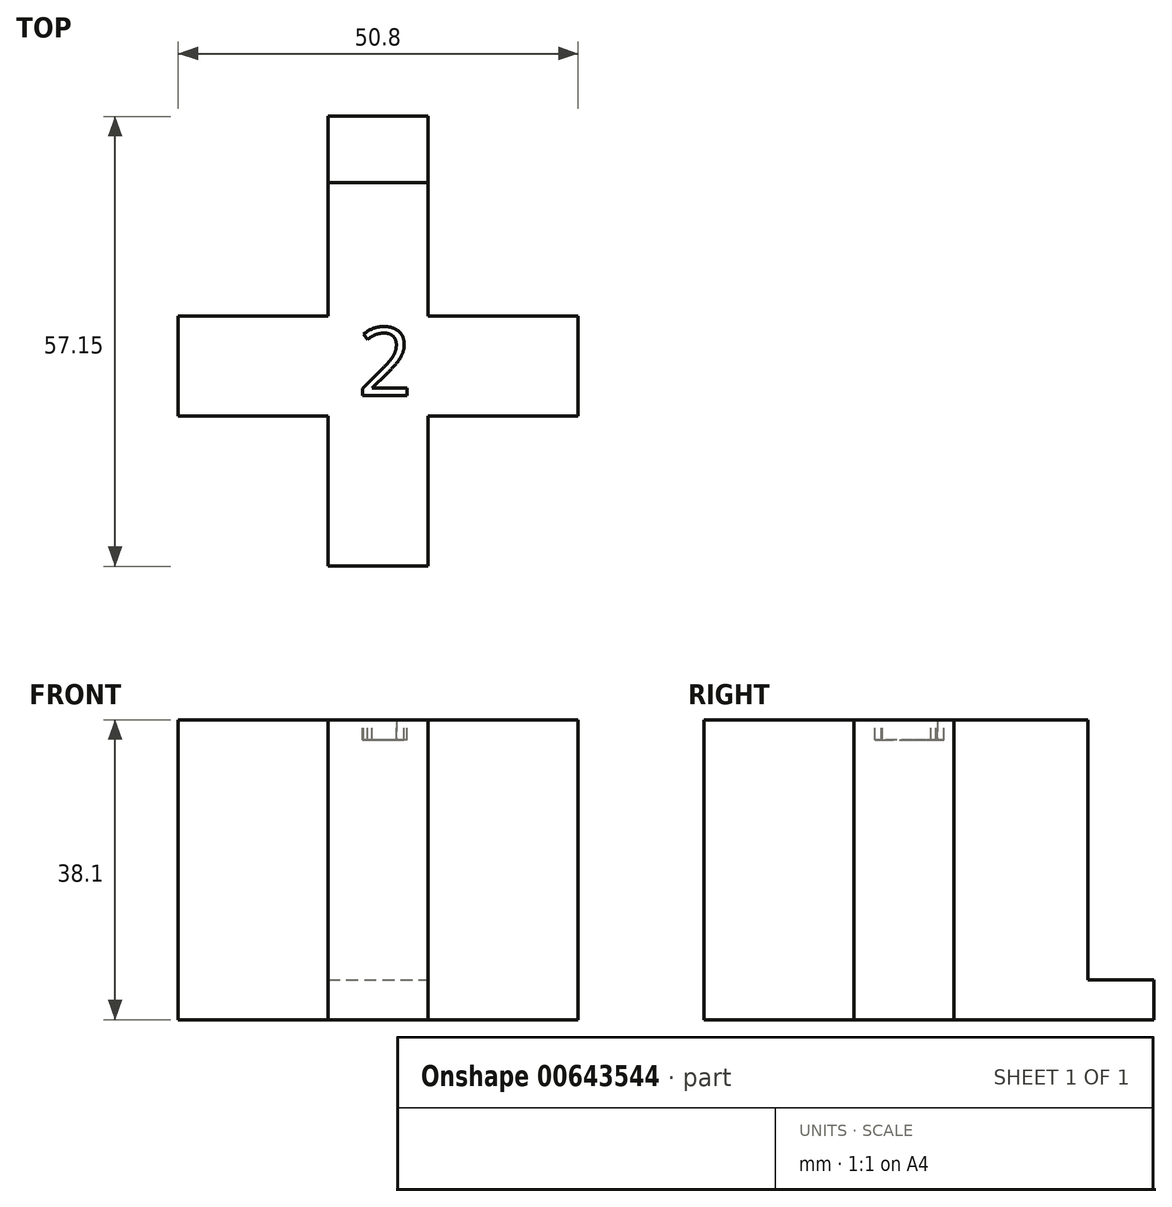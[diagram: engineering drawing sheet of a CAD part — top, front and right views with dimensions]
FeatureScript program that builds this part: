
annotation { "Feature Type Name" : "Feature", "Feature Type Description" : "" }
export const myFeature = defineFeature(function(context is Context, id is Id, definition is map)
    precondition{}
    {
        {
            var Q0;
            Q0=qCreatedBy(makeId("Top.planeOp"),FACE);
            var sketch = newSketch(context, id + "F0", { "sketchPlane" : qUnion([Q0])});
            skLineSegment(sketch, "E0.bottom", {"start": v(-43.37, 31.57) * mm, "end": v(-30.67, 31.57) * mm});
            skLineSegment(sketch, "E0.top", {"start": v(-43.37, -25.58) * mm, "end": v(-30.67, -25.58) * mm});
            skLineSegment(sketch, "E0.left", {"start": v(-43.37, 31.57) * mm, "end": v(-43.37, -25.58) * mm});
            skLineSegment(sketch, "E0.right", {"start": v(-30.67, 31.57) * mm, "end": v(-30.67, -25.58) * mm});
            skSolve(sketch);
        }
        {
            var Q0;
            Q0=qSketchRegion(id+"F0",true);
            extrude(context, id + "F1", {"entities" : qUnion([Q0]), "depth" : 5.08 * mm, "offsetDistance" : 25.4 * mm});
        }
        {
            var Q0;
            Q0=qCreatedBy(makeId("Top.planeOp"),FACE);
            var sketch = newSketch(context, id + "F2", { "sketchPlane" : qUnion([Q0])});
            skLineSegment(sketch, "E1.bottom", {"start": v(-62.42, -6.53) * mm, "end": v(-11.62, -6.53) * mm});
            skLineSegment(sketch, "E1.top", {"start": v(-62.42, 6.17) * mm, "end": v(-11.62, 6.17) * mm});
            skLineSegment(sketch, "E1.left", {"start": v(-62.42, -6.53) * mm, "end": v(-62.42, 6.17) * mm});
            skLineSegment(sketch, "E1.right", {"start": v(-11.62, -6.53) * mm, "end": v(-11.62, 6.17) * mm});
            skSolve(sketch);
        }
        {
            var Q0;
            Q0=qSketchRegion(id+"F2",true);
            extrude(context, id + "F3", {"entities" : qUnion([Q0]), "operationType" : NewBodyOperationType.ADD, "depth" : 38.1 * mm, "offsetDistance" : 25.4 * mm});
        }
        {
            var Q0;
            {var subQ0=sQuery(id+"F0.wireOp",EDGE,"E0.top");var subQ1=sQuery(id+"F0.wireOp",EDGE,"E0.left");var subQ2=sQuery(id+"F0.wireOp",EDGE,"E0.right");Q0=makeQuery(id+"F3.boolean.opBoolean","SPLIT",FACE,{"disambiguationData":[TD([makeQuery(id+"F1.opExtrude","SWEPT_FACE",FACE,{"disambiguationData":[OSD([subQ0])]})])],"derivedFrom":makeQuery(id+"F1.opExtrude","CAP_FACE",FACE,{"disambiguationData":[OSD([sQuery(id+"F0.wireOp",EDGE,"E0.bottom"),subQ0,subQ1,subQ2])],"isStart":false})});}
            var sketch = newSketch(context, id + "F4", { "sketchPlane" : qUnion([Q0])});
            skLineSegment(sketch, "E2.bottom", {"start": v(-30.67, -25.58) * mm, "end": v(-43.37, -25.58) * mm});
            skLineSegment(sketch, "E2.top", {"start": v(-30.67, 23.16) * mm, "end": v(-43.37, 23.16) * mm});
            skLineSegment(sketch, "E2.left", {"start": v(-30.67, -25.58) * mm, "end": v(-30.67, 23.16) * mm});
            skLineSegment(sketch, "E2.right", {"start": v(-43.37, -25.58) * mm, "end": v(-43.37, 23.16) * mm});
            skSolve(sketch);
        }
        {
            var Q0;
            Q0=qSketchRegion(id+"F4",true);
            extrude(context, id + "F5", {"entities" : qUnion([Q0]), "operationType" : NewBodyOperationType.ADD, "depth" : 33.02 * mm, "offsetDistance" : 25.4 * mm});
        }
        {
            var Q0;
            Q0=makeQuery(id+"F5.boolean.opBoolean","MERGE",FACE,{"derivedFrom":[makeQuery(id+"F3.opExtrude","CAP_FACE",FACE,{"disambiguationData":[OSD([sQuery(id+"F2.wireOp",EDGE,"E1.bottom"),sQuery(id+"F2.wireOp",EDGE,"E1.top"),sQuery(id+"F2.wireOp",EDGE,"E1.left"),sQuery(id+"F2.wireOp",EDGE,"E1.right")])],"isStart":false}),makeQuery(id+"F5.opExtrude","CAP_FACE",FACE,{"disambiguationData":[OSD([sQuery(id+"F4.wireOp",EDGE,"E2.bottom"),sQuery(id+"F4.wireOp",EDGE,"E2.top"),sQuery(id+"F4.wireOp",EDGE,"E2.left"),sQuery(id+"F4.wireOp",EDGE,"E2.right")])],"isStart":false})]});
            var sketch = newSketch(context, id + "F6", { "sketchPlane" : qUnion([Q0])});
            skText(sketch, "E3", { "text": "2", "fontName": "OpenSans-Regular.ttf"});
            const initialGuessF6  = {"E3": [-0.0396, -0.00387, 1, 0, 0.0087]};
            skSetInitialGuess(sketch, initialGuessF6);
            skSolve(sketch);
        }
        {
            var Q0;
            Q0=qSketchRegion(id+"F6",true);
            extrude(context, id + "F7", {"entities" : qUnion([Q0]), "operationType" : NewBodyOperationType.REMOVE, "oppositeDirection" : true, "depth" : 2.54 * mm, "offsetDistance" : 25.4 * mm});
        }
    });
